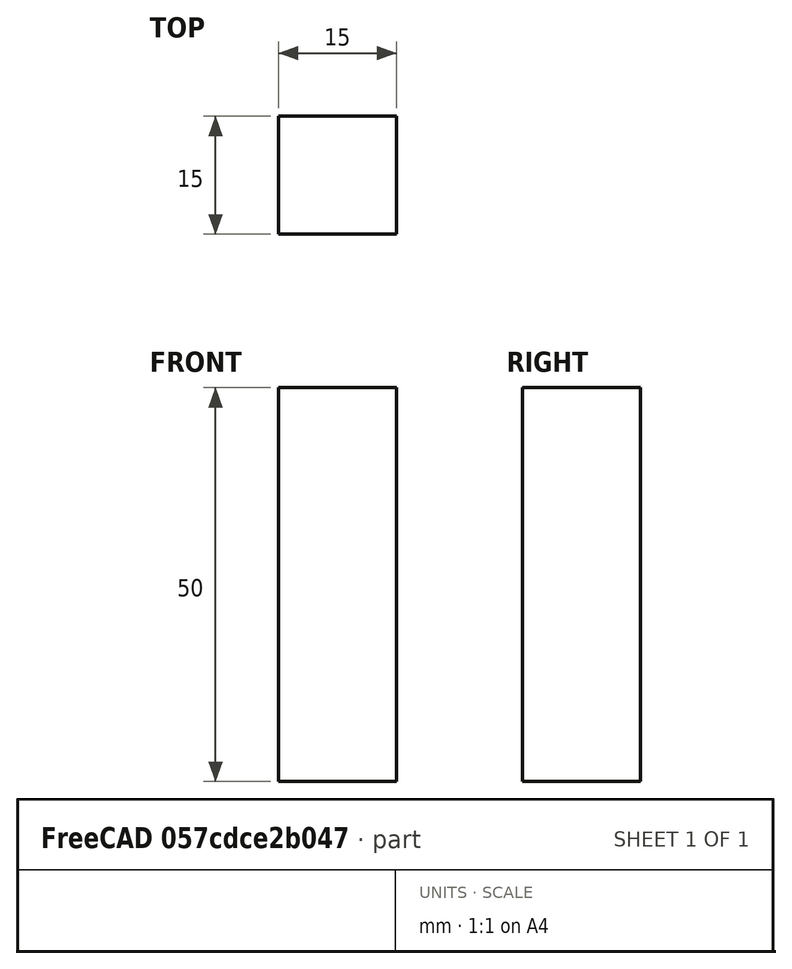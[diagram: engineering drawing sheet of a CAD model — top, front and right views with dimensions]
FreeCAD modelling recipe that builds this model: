
FCSTD DOCUMENT  (FreeCAD 0.15R4671 (Git))
Label: Square Bar 15 EN10059 S235JR
License: All rights reserved
LicenseURL: http://en.wikipedia.org/wiki/All_rights_reserved
objects: Sketcher::SketchObject×1, Part::Extrusion×1
note: 2 computed .brp shape members not serialized (recipe doc carries the construction recipe); baked Part::Feature solids carry a one-line shape summary decoded from their .brp

FEATURE [Sketcher::SketchObject] Sketch
  sketch-geometry (4):
    g0: LineSegment StartX=-7.5 StartY=-7.5 StartZ=0 EndX=7.5 EndY=-7.5 EndZ=0
    g1: LineSegment StartX=7.5 StartY=-7.5 StartZ=0 EndX=7.5 EndY=7.5 EndZ=0
    g2: LineSegment StartX=7.5 StartY=7.5 StartZ=0 EndX=-7.5 EndY=7.5 EndZ=0
    g3: LineSegment StartX=-7.5 StartY=7.5 StartZ=0 EndX=-7.5 EndY=-7.5 EndZ=0
  constraints (12):
    c: Coincident(g0,g1)
    c: Coincident(g1,g2)
    c: Coincident(g2,g3)
    c: Coincident(g3,g0)
    c: Horizontal(g0)
    c: Horizontal(g2)
    c: Vertical(g1)
    c: Vertical(g3)
    c: Symmetric(g1,g0,g-1)
    c: Symmetric(g2,g1,g-2)
    c: Equal(g1,g2)
    c: DistanceY(g1) = 15
FEATURE [Part::Extrusion] Extrude  label="Square Bar 15 EN10059 S235JR"
  Base = -> Sketch
  Dir = (0,0,50)
  Solid = true
